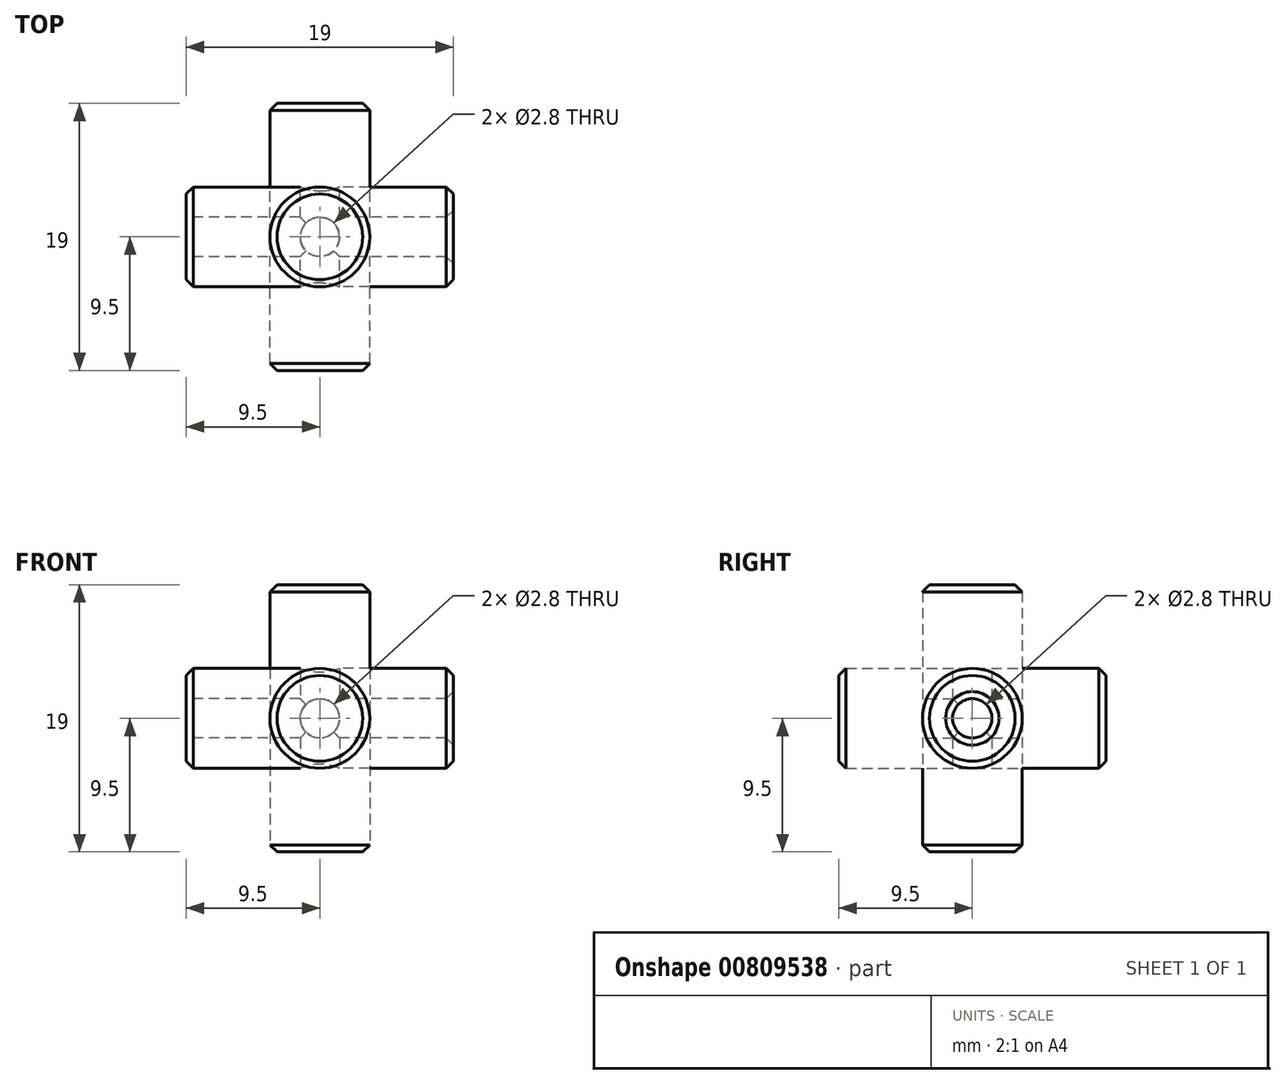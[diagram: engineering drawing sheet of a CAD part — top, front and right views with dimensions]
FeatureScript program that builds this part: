
annotation { "Feature Type Name" : "Feature", "Feature Type Description" : "" }
export const myFeature = defineFeature(function(context is Context, id is Id, definition is map)
    precondition{}
    {
        {
            var Q0;
            Q0=qCreatedBy(makeId("Front.planeOp"),FACE);
            var sketch = newSketch(context, id + "F0", { "sketchPlane" : qUnion([Q0])});
            skCircle(sketch, "E0", {"center": v(0, 0) * mm, "radius": 3.55 * mm});
            skSolve(sketch);
        }
        {
            var Q0;
            Q0 = qSketchRegion(id + "F0", true);
            extrude(context, id + "F1", {"entities" : qUnion([Q0]), "endBound" : BoundingType.SYMMETRIC, "depth" : 19 * mm, "offsetDistance" : 25 * mm});
        }
        {
            var Q0;
            Q0=qCreatedBy(makeId("Front.planeOp"),FACE);
            var sketch = newSketch(context, id + "F2", { "sketchPlane" : qUnion([Q0])});
            skCircle(sketch, "E1", {"center": v(0, 0) * mm, "radius": 1.4 * mm});
            skSolve(sketch);
        }
        {
            var Q0;
            Q0 = qSketchRegion(id + "F2", true);
            extrude(context, id + "F3", {"entities" : qUnion([Q0]), "endBound" : BoundingType.SYMMETRIC, "depth" : 20 * mm, "offsetDistance" : 25 * mm});
        }
        {
            var Q0;
            Q0=qCreatedBy(makeId("Front.planeOp"),FACE);
            var sketch = newSketch(context, id + "F4", { "sketchPlane" : qUnion([Q0])});
            skLineSegment(sketch, "E2.bottom", {"start": v(0, 0) * mm, "end": v(10, 0) * mm});
            skLineSegment(sketch, "E2.top", {"start": v(0, 10) * mm, "end": v(10, 10) * mm});
            skLineSegment(sketch, "E2.left", {"start": v(0, 0) * mm, "end": v(0, 10) * mm});
            skLineSegment(sketch, "E2.right", {"start": v(10, 0) * mm, "end": v(10, 10) * mm});
            skSolve(sketch);
        }
        {
            var Q0;
            Q0 = qSketchRegion(id + "F4", true);
            extrude(context, id + "F5", {"entities" : qUnion([Q0]), "depth" : 10 * mm, "offsetDistance" : 25 * mm});
        }
        {
            var Q0;
            Q0=qCreatedBy(makeId("Origin.pointOp"),VERTEX);
            var Q1;
            Q1=makeQuery(id+"F5.opExtrude","CAP_VERTEX",VERTEX,{"disambiguationData":[OSD([sQuery(id+"F4.wireOp",EDGE,"E2.top"),sQuery(id+"F4.wireOp",EDGE,"E2.right")])],"isStart":false});
            var Q2;
            Q2=makeQuery(id+"F5.opExtrude","CAP_VERTEX",VERTEX,{"disambiguationData":[OSD([sQuery(id+"F4.wireOp",EDGE,"E2.bottom"),sQuery(id+"F4.wireOp",EDGE,"E2.right")])],"isStart":false});
            cPlane(context, id + "F6", {"entities" : qUnion([Q0, Q1, Q2]), "cplaneType" : CPlaneType.THREE_POINT, "offset" : 25 * mm, "width" : 150 * mm, "height" : 150 * mm});
        }
        {
            var Q0;
            Q0=qCreatedBy(id+"F6.planeOp",FACE);
            var sketch = newSketch(context, id + "F7", { "sketchPlane" : qUnion([Q0])});
            skLineSegment(sketch, "E3", {"start": v(0, 0) * mm, "end": v(14.14, 10) * mm});
            skSolve(sketch);
        }
        {
            var Q0;
            Q0=makeQuery(id+"F5.opExtrude","SWEPT_BODY",BODY,{"disambiguationData":[OSD([sQuery(id+"F4.wireOp",EDGE,"E2.bottom"),sQuery(id+"F4.wireOp",EDGE,"E2.top"),sQuery(id+"F4.wireOp",EDGE,"E2.left"),sQuery(id+"F4.wireOp",EDGE,"E2.right")])]});
            deleteBodies(context, id + "F8", {"entities" : qUnion([Q0])});
        }
        {
            var Q0;
            Q0=makeQuery(id+"F3.opExtrude","SWEPT_BODY",BODY,{"disambiguationData":[OSD([sQuery(id+"F2.wireOp",EDGE,"E1")])]});
            var Q1;
            Q1=makeQuery(id+"F1.opExtrude","SWEPT_BODY",BODY,{"disambiguationData":[OSD([sQuery(id+"F0.wireOp",EDGE,"E0")])]});
            var Q2;
            Q2=sQuery(id+"F7.wireOp",EDGE,"E3");
            circularPattern(context, id + "F9", {"entities" : qUnion([Q0, Q1]), "axis" : qUnion([Q2]), "angle" : 360 * degree, "instanceCount" : 3, "equalSpace" : true});
        }
        {
            var Q0;
            Q0=makeQuery(id+"F9.opPattern","COPY",BODY,{"derivedFrom":makeQuery(id+"F3.opExtrude","SWEPT_BODY",BODY,{"disambiguationData":[OSD([sQuery(id+"F2.wireOp",EDGE,"E1")])]}),"instanceName":"1"});
            var Q1;
            Q1=makeQuery(id+"F3.opExtrude","SWEPT_BODY",BODY,{"disambiguationData":[OSD([sQuery(id+"F2.wireOp",EDGE,"E1")])]});
            var Q2;
            Q2=makeQuery(id+"F9.opPattern","COPY",BODY,{"derivedFrom":makeQuery(id+"F3.opExtrude","SWEPT_BODY",BODY,{"disambiguationData":[OSD([sQuery(id+"F2.wireOp",EDGE,"E1")])]}),"instanceName":"2"});
            var Q3;
            Q3=makeQuery(id+"F9.opPattern","COPY",BODY,{"derivedFrom":makeQuery(id+"F1.opExtrude","SWEPT_BODY",BODY,{"disambiguationData":[OSD([sQuery(id+"F0.wireOp",EDGE,"E0")])]}),"instanceName":"1"});
            booleanBodies(context, id + "F10", {"operationType" : BooleanOperationType.SUBTRACTION, "tools" : qUnion([Q0, Q1, Q2]), "targets" : qUnion([Q3])});
        }
        {
            var Q0;
            Q0=makeQuery(id+"F9.opPattern","COPY",FACE,{"derivedFrom":makeQuery(id+"F1.opExtrude","CAP_FACE",FACE,{"disambiguationData":[OSD([sQuery(id+"F0.wireOp",EDGE,"E0")])],"isStart":true}),"instanceName":"2"});
            var Q1;
            Q1=makeQuery(id+"F9.opPattern","COPY",FACE,{"derivedFrom":makeQuery(id+"F1.opExtrude","CAP_FACE",FACE,{"disambiguationData":[OSD([sQuery(id+"F0.wireOp",EDGE,"E0")])],"isStart":false}),"instanceName":"1"});
            var Q2;
            Q2=makeQuery(id+"F1.opExtrude","CAP_FACE",FACE,{"disambiguationData":[OSD([sQuery(id+"F0.wireOp",EDGE,"E0")])],"isStart":false});
            var Q3;
            Q3=makeQuery(id+"F9.opPattern","COPY",FACE,{"derivedFrom":makeQuery(id+"F1.opExtrude","CAP_FACE",FACE,{"disambiguationData":[OSD([sQuery(id+"F0.wireOp",EDGE,"E0")])],"isStart":false}),"instanceName":"2"});
            var Q4;
            Q4=makeQuery(id+"F1.opExtrude","CAP_FACE",FACE,{"disambiguationData":[OSD([sQuery(id+"F0.wireOp",EDGE,"E0")])],"isStart":true});
            var Q5;
            Q5=makeQuery(id+"F9.opPattern","COPY",EDGE,{"derivedFrom":makeQuery(id+"F1.opExtrude","CAP_EDGE",EDGE,{"disambiguationData":[OSD([sQuery(id+"F0.wireOp",EDGE,"E0")])],"isStart":true}),"instanceName":"1"});
            chamfer(context, id + "F11", {"entities" : qUnion([Q0, Q1, Q2, Q3, Q4, Q5]), "width" : 0.5 * mm, "tangentPropagation" : true});
        }
    });
